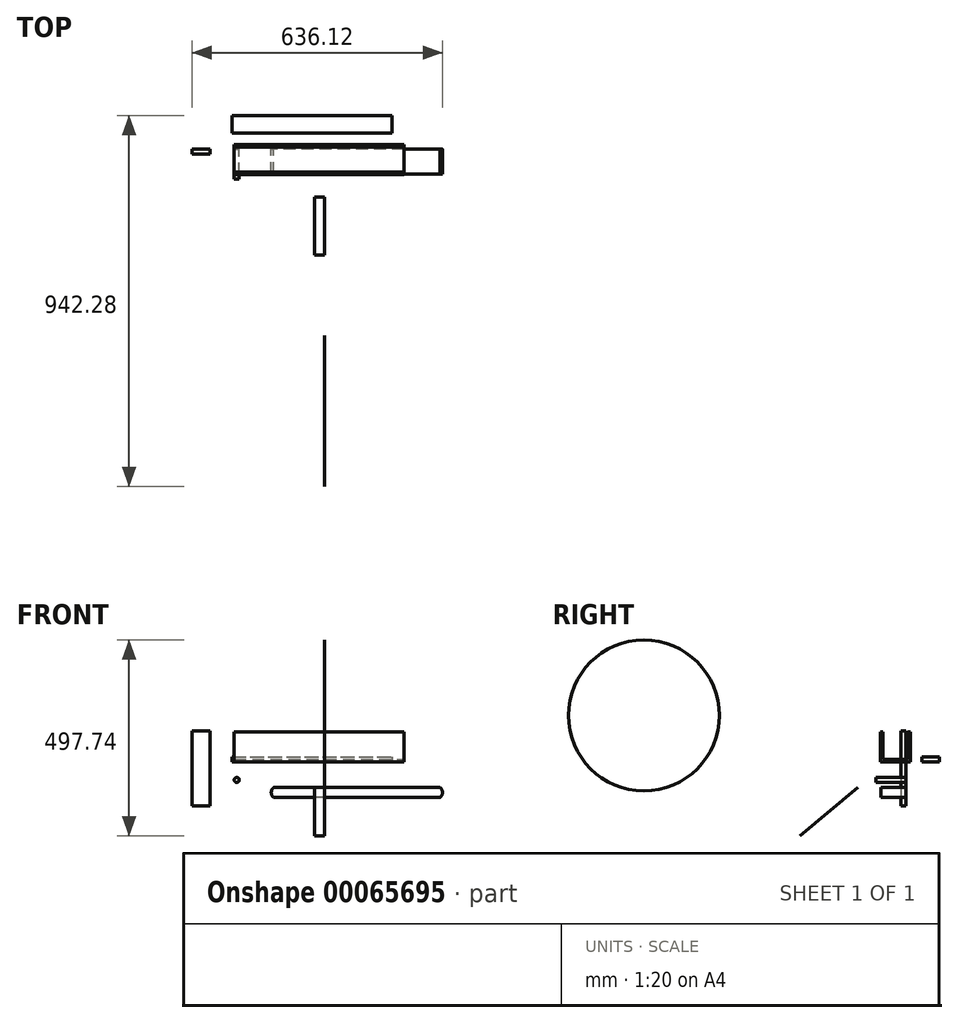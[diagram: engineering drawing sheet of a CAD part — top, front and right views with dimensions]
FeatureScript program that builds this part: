
annotation { "Feature Type Name" : "Feature", "Feature Type Description" : "" }
export const myFeature = defineFeature(function(context is Context, id is Id, definition is map)
    precondition{}
    {
        {
            var Q0;
            Q0=qCreatedBy(makeId("Top.planeOp"),FACE);
            var sketch = newSketch(context, id + "F0", { "sketchPlane" : qUnion([Q0])});
            skLineSegment(sketch, "E0.bottom", {"start": v(-203.52, 11.12) * mm, "end": v(228.28, 11.12) * mm});
            skLineSegment(sketch, "E0.top", {"start": v(-203.52, -65.08) * mm, "end": v(228.28, -65.08) * mm});
            skLineSegment(sketch, "E0.left", {"start": v(-203.52, 11.12) * mm, "end": v(-203.52, -65.08) * mm});
            skLineSegment(sketch, "E0.right", {"start": v(228.28, 11.12) * mm, "end": v(228.28, -65.08) * mm});
            skSolve(sketch);
        }
        {
            var Q0;
            Q0=makeQuery(id+"F0.imprint","IMPRINT",FACE,{"disambiguationData":[TD([[makeQuery(id+"F0.imprint","IMPRINT",EDGE,{"derivedFrom":sQuery(id+"F0.wireOp",EDGE,"E0.bottom")}),-1.0]])]});
            extrude(context, id + "F1", {"entities" : qUnion([Q0]), "depth" : 6.35 * mm});
        }
        {
            var Q0;
            Q0=makeQuery(id+"F1.opExtrude","CAP_FACE",FACE,{"disambiguationData":[OSD([sQuery(id+"F0.wireOp",EDGE,"E0.bottom"),sQuery(id+"F0.wireOp",EDGE,"E0.top"),sQuery(id+"F0.wireOp",EDGE,"E0.left"),sQuery(id+"F0.wireOp",EDGE,"E0.right")])],"isStart":false});
            var sketch = newSketch(context, id + "F2", { "sketchPlane" : qUnion([Q0])});
            skLineSegment(sketch, "E1.bottom", {"start": v(-203.52, 11.12) * mm, "end": v(228.28, 11.12) * mm});
            skLineSegment(sketch, "E1.top", {"start": v(-203.52, 4.77) * mm, "end": v(228.28, 4.77) * mm});
            skLineSegment(sketch, "E1.left", {"start": v(-203.52, 11.12) * mm, "end": v(-203.52, 4.77) * mm});
            skLineSegment(sketch, "E1.right", {"start": v(228.28, 11.12) * mm, "end": v(228.28, 4.77) * mm});
            skLineSegment(sketch, "E2.bottom", {"start": v(-203.52, -65.08) * mm, "end": v(228.28, -65.08) * mm});
            skLineSegment(sketch, "E2.top", {"start": v(-203.52, -58.73) * mm, "end": v(228.28, -58.73) * mm});
            skLineSegment(sketch, "E2.left", {"start": v(-203.52, -65.08) * mm, "end": v(-203.52, -58.73) * mm});
            skLineSegment(sketch, "E2.right", {"start": v(228.28, -65.08) * mm, "end": v(228.28, -58.73) * mm});
            skSolve(sketch);
        }
        {
            var Q0;
            Q0=makeQuery(id+"F2.imprint","IMPRINT",FACE,{"disambiguationData":[TD([[makeQuery(id+"F2.imprint","IMPRINT",EDGE,{"derivedFrom":sQuery(id+"F2.wireOp",EDGE,"E1.bottom")}),-1.0]])]});
            var Q1;
            Q1=makeQuery(id+"F2.imprint","IMPRINT",FACE,{"disambiguationData":[TD([[makeQuery(id+"F2.imprint","IMPRINT",EDGE,{"derivedFrom":sQuery(id+"F2.wireOp",EDGE,"E2.bottom")}),1.0]])]});
            extrude(context, id + "F3", {"entities" : qUnion([Q0, Q1]), "operationType" : NewBodyOperationType.ADD, "depth" : 69.85 * mm});
        }
        {
            var Q0;
            Q0=qCreatedBy(makeId("Top.planeOp"),FACE);
            var sketch = newSketch(context, id + "F4", { "sketchPlane" : qUnion([Q0])});
            skLineSegment(sketch, "E3.bottom", {"start": v(-209.15, 84.64) * mm, "end": v(197.25, 84.64) * mm});
            skLineSegment(sketch, "E3.top", {"start": v(-209.15, 40.2) * mm, "end": v(197.25, 40.2) * mm});
            skLineSegment(sketch, "E3.left", {"start": v(-209.15, 84.64) * mm, "end": v(-209.15, 40.2) * mm});
            skLineSegment(sketch, "E3.right", {"start": v(197.25, 84.64) * mm, "end": v(197.25, 40.2) * mm});
            skSolve(sketch);
        }
        {
            var Q0;
            Q0=makeQuery(id+"F4.imprint","IMPRINT",FACE,{"disambiguationData":[TD([[makeQuery(id+"F4.imprint","IMPRINT",EDGE,{"derivedFrom":sQuery(id+"F4.wireOp",EDGE,"E3.bottom")}),-1.0]])]});
            extrude(context, id + "F5", {"entities" : qUnion([Q0]), "depth" : 12.7 * mm});
        }
        {
            var Q0;
            Q0=qCreatedBy(makeId("Front.planeOp"),FACE);
            var sketch = newSketch(context, id + "F6", { "sketchPlane" : qUnion([Q0])});
            skCircle(sketch, "E4", {"center": v(-197.12, -45.93) * mm, "radius": 6.35 * mm});
            skSolve(sketch);
        }
        {
            var Q0;
            Q0=makeQuery(id+"F6.imprint","IMPRINT",FACE,{"disambiguationData":[TD([[makeQuery(id+"F6.imprint","IMPRINT",EDGE,{"derivedFrom":sQuery(id+"F6.wireOp",EDGE,"E4")}),1.0]])]});
            extrude(context, id + "F7", {"entities" : qUnion([Q0]), "depth" : 76.2 * mm});
        }
        {
            var Q0;
            Q0=qCreatedBy(makeId("Front.planeOp"),FACE);
            var sketch = newSketch(context, id + "F8", { "sketchPlane" : qUnion([Q0])});
            skLineSegment(sketch, "E5", {"start": v(319.42, -65) * mm, "end": v(-103.51, -65) * mm});
            skArc(sketch, "E6", {"start": v(319.42, -90.4) * mm, "mid": v(325.53, -77.7) * mm, "end": v(319.42, -65) * mm});
            skLineSegment(sketch, "E7", {"start": v(319.42, -90.4) * mm, "end": v(-103.14, -90.4) * mm});
            skArc(sketch, "E8", {"start": v(-103.51, -65) * mm, "mid": v(-109.44, -77.8) * mm, "end": v(-103.14, -90.4) * mm});
            skSolve(sketch);
        }
        {
            var Q0;
            Q0=makeQuery(id+"F8.imprint","IMPRINT",FACE,{"disambiguationData":[TD([[makeQuery(id+"F8.imprint","IMPRINT",EDGE,{"derivedFrom":sQuery(id+"F8.wireOp",EDGE,"E5")}),1.0]])]});
            var Q1;
            Q1=sQuery(id+"F8.wireOp",EDGE,"E5");
            var Q2;
            Q2=sQuery(id+"F8.wireOp",EDGE,"E8");
            var Q3;
            Q3=sQuery(id+"F8.wireOp",EDGE,"E7");
            var Q4;
            Q4=sQuery(id+"F8.wireOp",EDGE,"E6");
            extrude(context, id + "F9", {"entities" : qUnion([Q0]), "surfaceEntities" : qUnion([Q1, Q2, Q3, Q4]), "depth" : 63.5 * mm});
        }
        {
            var Q0;
            Q0=qCreatedBy(makeId("Front.planeOp"),FACE);
            var sketch = newSketch(context, id + "F10", { "sketchPlane" : qUnion([Q0])});
            skLineSegment(sketch, "E9.bottom", {"start": v(-310.6, 78.94) * mm, "end": v(-264.45, 78.94) * mm});
            skLineSegment(sketch, "E9.top", {"start": v(-310.6, -111.56) * mm, "end": v(-264.45, -111.56) * mm});
            skLineSegment(sketch, "E9.left", {"start": v(-310.6, 78.94) * mm, "end": v(-310.6, -111.56) * mm});
            skLineSegment(sketch, "E9.right", {"start": v(-264.45, 78.94) * mm, "end": v(-264.45, -111.56) * mm});
            skSolve(sketch);
        }
        {
            var Q0;
            Q0=makeQuery(id+"F10.imprint","IMPRINT",FACE,{"disambiguationData":[TD([[makeQuery(id+"F10.imprint","IMPRINT",EDGE,{"derivedFrom":sQuery(id+"F10.wireOp",EDGE,"E9.bottom")}),-1.0]])]});
            extrude(context, id + "F11", {"entities" : qUnion([Q0]), "depth" : 12.7 * mm});
        }
        {
            var Q0;
            Q0=qCreatedBy(makeId("Right.planeOp"),FACE);
            var sketch = newSketch(context, id + "F12", { "sketchPlane" : qUnion([Q0])});
            skLineSegment(sketch, "E10", {"start": v(-269.58, -187.78) * mm, "end": v(-269.58, -188.03) * mm});
            skLineSegment(sketch, "E11", {"start": v(-269.58, -188.03) * mm, "end": v(-122.25, -65.28) * mm});
            skLineSegment(sketch, "E12", {"start": v(-122.25, -65.28) * mm, "end": v(-122.25, -65.02) * mm});
            skLineSegment(sketch, "E13", {"start": v(-122.25, -65.02) * mm, "end": v(-269.58, -187.78) * mm});
            skSolve(sketch);
        }
        {
            var Q0;
            Q0 = qSketchRegion(id + "F12", true);
            extrude(context, id + "F13", {"entities" : qUnion([Q0]), "operationType" : NewBodyOperationType.ADD, "depth" : 25.4 * mm});
        }
        {
            var Q0;
            Q0=makeQuery(id+"F13.opExtrude","CAP_FACE",FACE,{"disambiguationData":[OSD([sQuery(id+"F12.wireOp",EDGE,"E10"),sQuery(id+"F12.wireOp",EDGE,"E11"),sQuery(id+"F12.wireOp",EDGE,"E12"),sQuery(id+"F12.wireOp",EDGE,"E13")])],"isStart":false});
            var sketch = newSketch(context, id + "F14", { "sketchPlane" : qUnion([Q0])});
            skCircle(sketch, "E14", {"center": v(-665.87, 117.94) * mm, "radius": 191.77 * mm});
            skSolve(sketch);
        }
        {
            var Q0;
            Q0=makeQuery(id+"F14.imprint","IMPRINT",FACE,{"disambiguationData":[TD([[makeQuery(id+"F14.imprint","IMPRINT",EDGE,{"derivedFrom":sQuery(id+"F14.wireOp",EDGE,"E14")}),1.0]])]});
            extrude(context, id + "F15", {"entities" : qUnion([Q0]), "depth" : 0.25 * mm});
        }
    });
